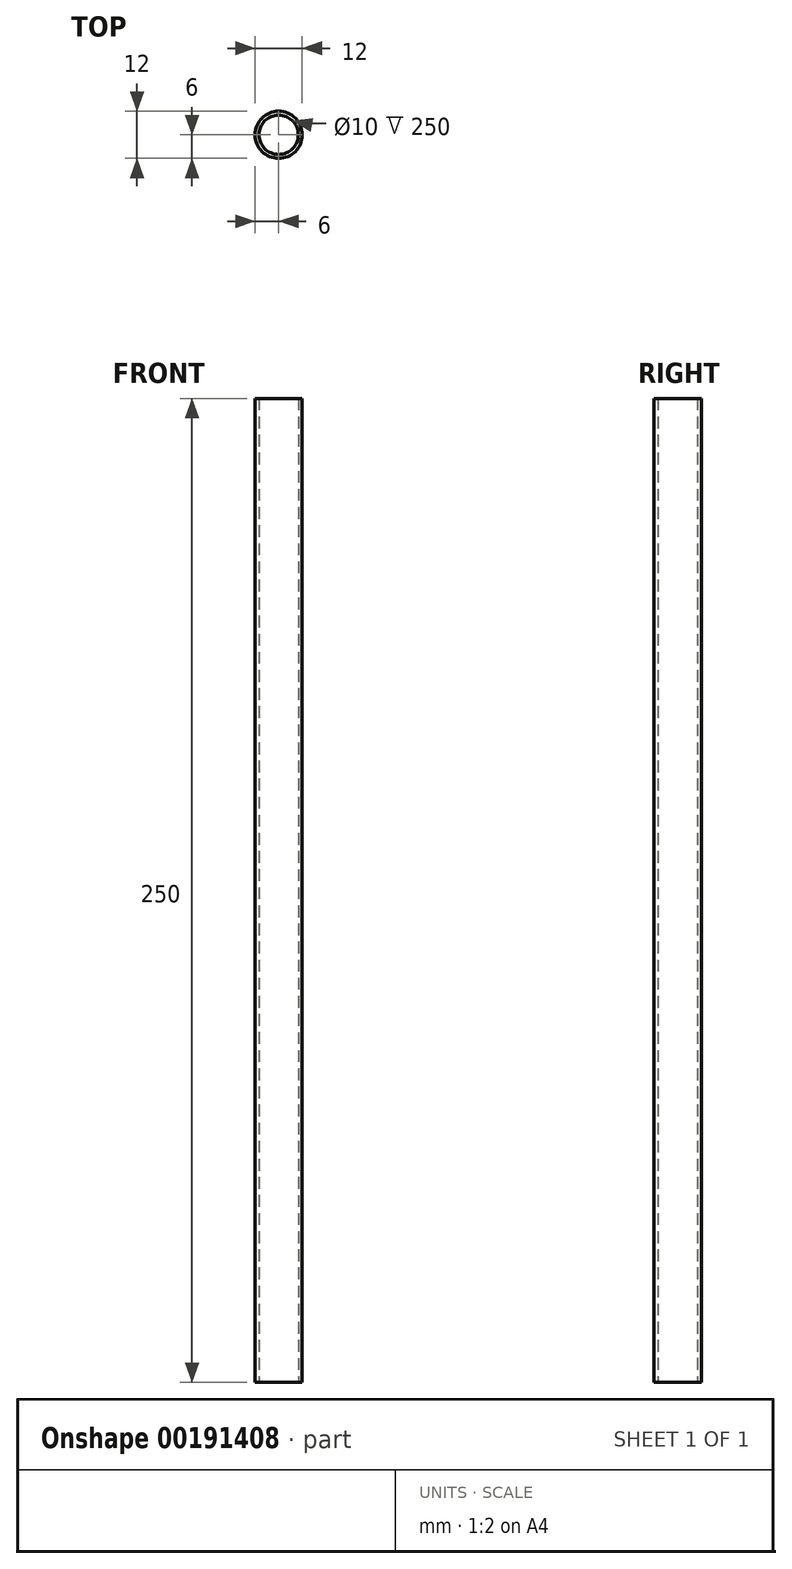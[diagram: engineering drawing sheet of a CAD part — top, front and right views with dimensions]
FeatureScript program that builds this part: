
annotation { "Feature Type Name" : "Feature", "Feature Type Description" : "" }
export const myFeature = defineFeature(function(context is Context, id is Id, definition is map)
    precondition{}
    {
        {
            var Q0;
            Q0=qCreatedBy(makeId("Top.planeOp"),FACE);
            var sketch = newSketch(context, id + "F0", { "sketchPlane" : qUnion([Q0])});
            skCircle(sketch, "E0", {"center": v(0, 0) * mm, "radius": 6 * mm});
            skCircle(sketch, "E1", {"center": v(0, 0) * mm, "radius": 5 * mm});
            skSolve(sketch);
        }
        {
            var Q0;
            Q0=makeQuery(id+"F0.imprint","IMPRINT",FACE,{"disambiguationData":[TD([[makeQuery(id+"F0.imprint","IMPRINT",EDGE,{"derivedFrom":sQuery(id+"F0.wireOp",EDGE,"E0")}),1.0]])]});
            extrude(context, id + "F1", {"entities" : qUnion([Q0]), "depth" : 250 * mm});
        }
    });
